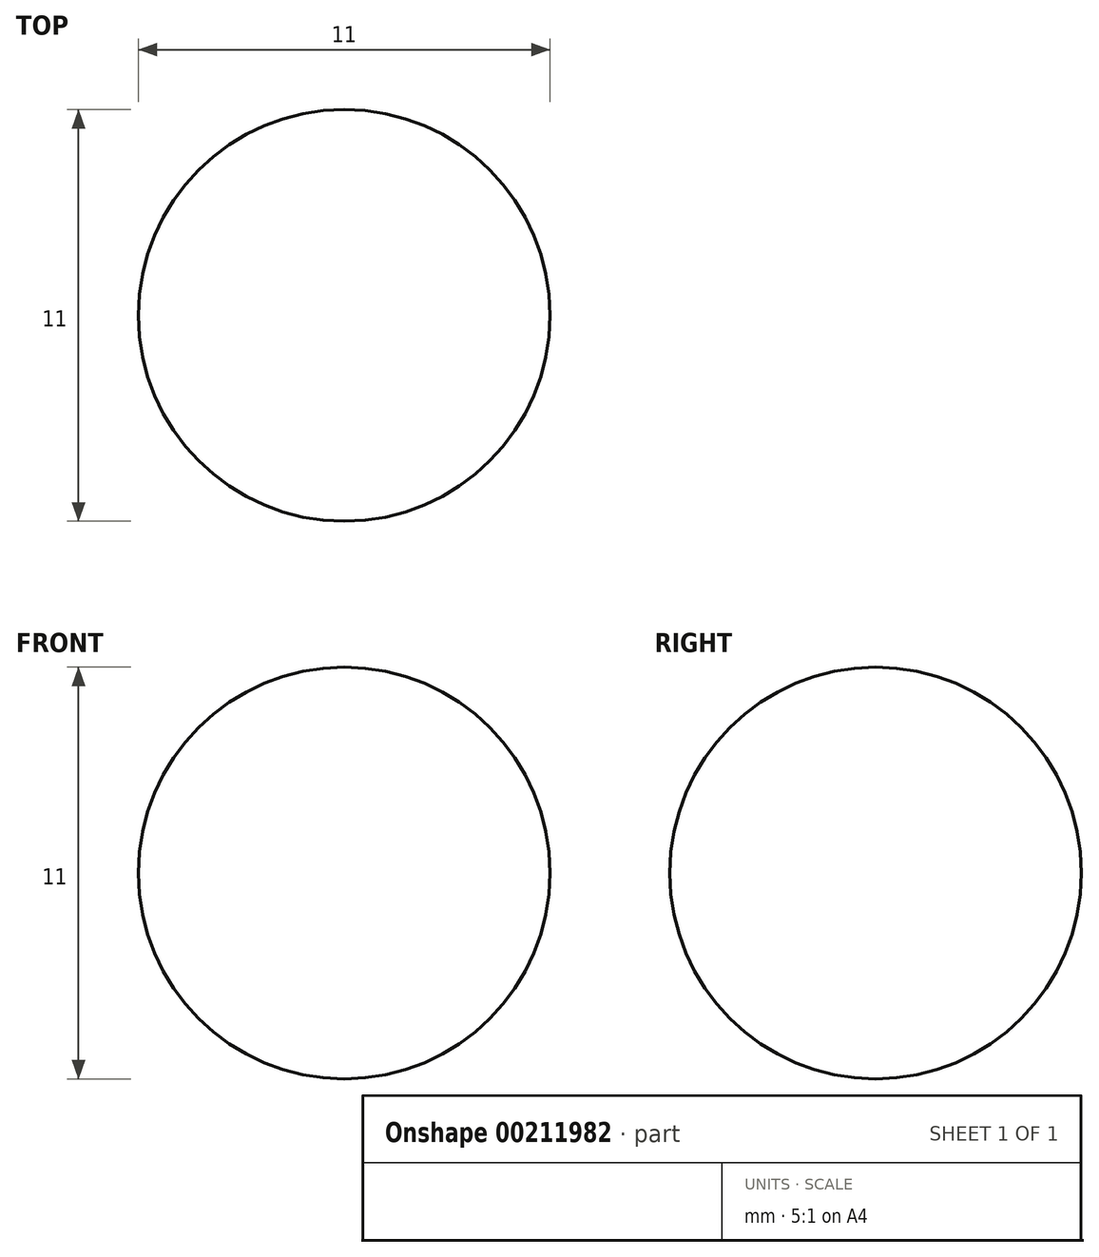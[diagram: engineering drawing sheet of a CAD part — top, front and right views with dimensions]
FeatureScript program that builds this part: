
annotation { "Feature Type Name" : "Feature", "Feature Type Description" : "" }
export const myFeature = defineFeature(function(context is Context, id is Id, definition is map)
    precondition{}
    {
        {
            var Q0;
            Q0=qCreatedBy(makeId("Front.planeOp"),FACE);
            var sketch = newSketch(context, id + "F0", { "sketchPlane" : qUnion([Q0])});
            skLineSegment(sketch, "E0", {"start": v(-23.89, 0) * mm, "end": v(19.12, 0) * mm, "construction": true});
            skCircle(sketch, "E1", {"center": v(0, 0) * mm, "radius": 5.5 * mm});
            skSolve(sketch);
        }
        {
            var Q0;
            Q0 = qSketchRegion(id + "F0", true);
            extrude(context, id + "F1", {"entities" : qUnion([Q0]), "depth" : 11 * mm});
        }
        {
            var Q0;
            Q0=makeQuery(id+"F1.opExtrude","CAP_EDGE",EDGE,{"disambiguationData":[OSD([sQuery(id+"F0.wireOp",EDGE,"E1")])],"isStart":false});
            var Q1;
            Q1=makeQuery(id+"F1.opExtrude","CAP_EDGE",EDGE,{"disambiguationData":[OSD([sQuery(id+"F0.wireOp",EDGE,"E1")])],"isStart":true});
            fillet(context, id + "F2", {"entities" : qUnion([Q0, Q1]), "radius" : (11 / 2) * mm, "tangentPropagation" : true, "allowEdgeOverflow" : false});
        }
    });
